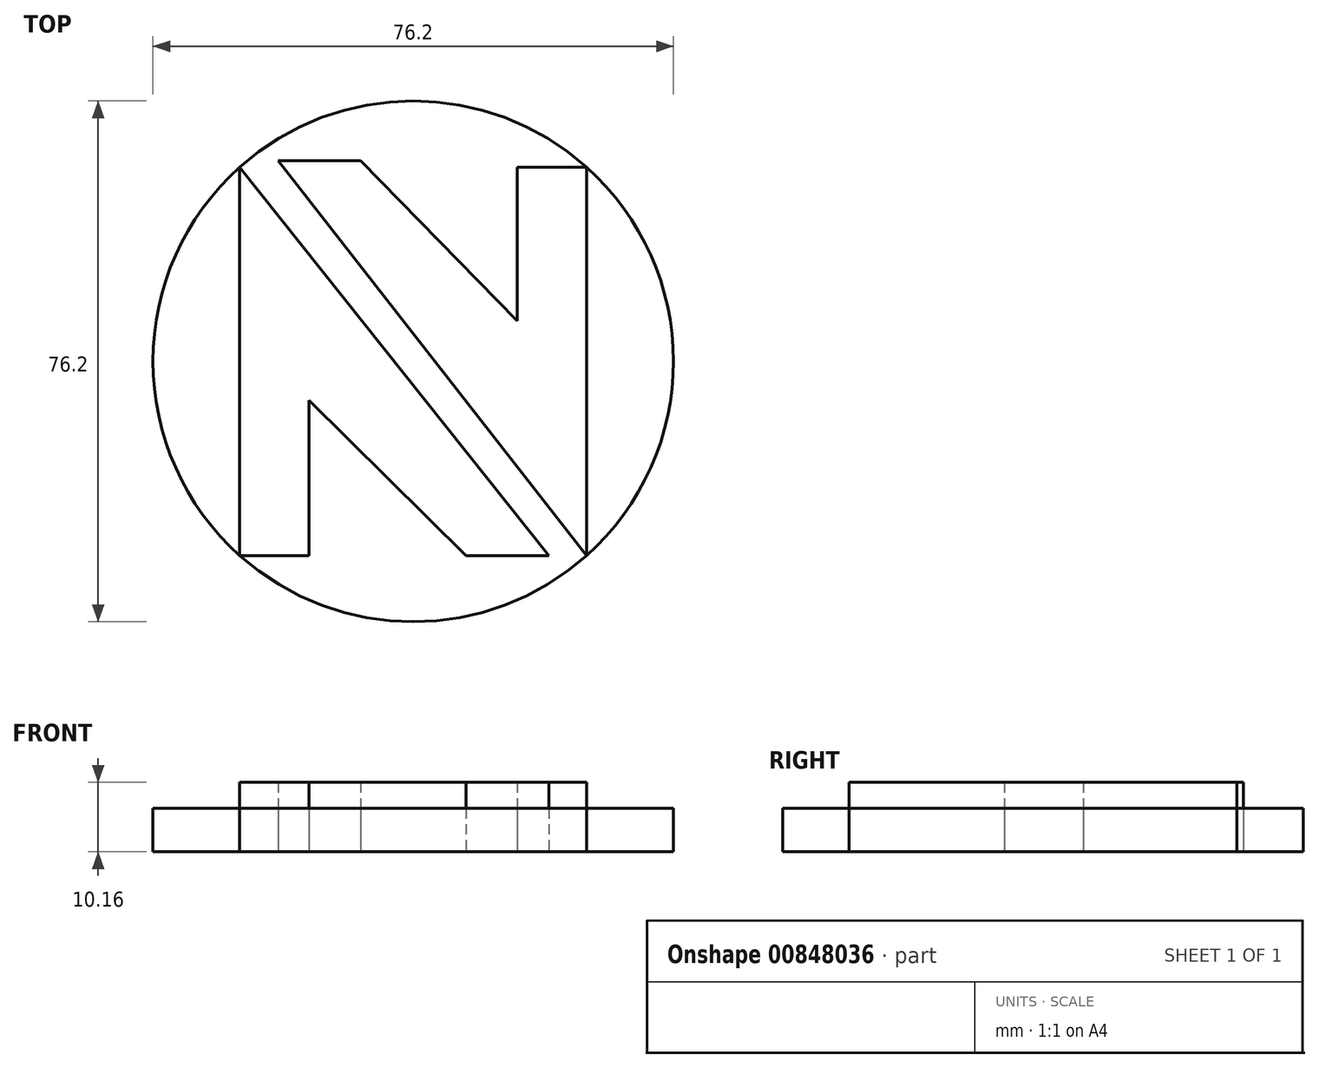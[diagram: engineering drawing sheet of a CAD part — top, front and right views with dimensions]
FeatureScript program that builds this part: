
annotation { "Feature Type Name" : "Feature", "Feature Type Description" : "" }
export const myFeature = defineFeature(function(context is Context, id is Id, definition is map)
    precondition{}
    {
        {
            var Q0;
            Q0=qCreatedBy(makeId("Top.planeOp"),FACE);
            var sketch = newSketch(context, id + "F0", { "sketchPlane" : qUnion([Q0])});
            skCircle(sketch, "E0", {"center": v(0, 0) * mm, "radius": 38.1 * mm});
            skLineSegment(sketch, "E1", {"start": v(-25.4, 28.4) * mm, "end": v(-25.4, -28.4) * mm});
            skLineSegment(sketch, "E2", {"start": v(-15.24, -5.68) * mm, "end": v(-15.24, -28.4) * mm});
            skLineSegment(sketch, "E3", {"start": v(-15.24, -28.4) * mm, "end": v(-25.4, -28.4) * mm});
            skLineSegment(sketch, "E4", {"start": v(-25.4, 28.4) * mm, "end": v(19.83, -28.4) * mm});
            skLineSegment(sketch, "E5", {"start": v(19.83, -28.4) * mm, "end": v(7.76, -28.4) * mm});
            skLineSegment(sketch, "E6", {"start": v(7.76, -28.4) * mm, "end": v(-15.24, -5.68) * mm});
            skLineSegment(sketch, "E7", {"start": v(25.4, -28.4) * mm, "end": v(25.4, 28.4) * mm});
            skLineSegment(sketch, "E8", {"start": v(25.4, -28.4) * mm, "end": v(-19.76, 29.33) * mm});
            skLineSegment(sketch, "E9", {"start": v(-19.76, 29.33) * mm, "end": v(-7.7, 29.33) * mm});
            skLineSegment(sketch, "E10", {"start": v(-7.7, 29.33) * mm, "end": v(15.24, 5.9) * mm});
            skLineSegment(sketch, "E11", {"start": v(15.24, 5.9) * mm, "end": v(15.24, 28.4) * mm});
            skLineSegment(sketch, "E12", {"start": v(15.24, 28.4) * mm, "end": v(25.4, 28.4) * mm});
            skSolve(sketch);
        }
        {
            var Q0;
            Q0=makeQuery(id+"F0.imprint","IMPRINT",FACE,{"disambiguationData":[TD([[makeQuery(id+"F0.imprint","IMPRINT",EDGE,{"derivedFrom":sQuery(id+"F0.wireOp",EDGE,"E7")}),1.0]])]});
            var Q1;
            Q1=makeQuery(id+"F0.imprint","IMPRINT",FACE,{"disambiguationData":[TD([[makeQuery(id+"F0.imprint","IMPRINT",EDGE,{"derivedFrom":sQuery(id+"F0.wireOp",EDGE,"E1")}),1.0]])]});
            extrude(context, id + "F1", {"entities" : qUnion([Q0, Q1]), "depth" : 10.16 * mm, "offsetDistance" : 25.4 * mm});
        }
        {
            var Q0;
            Q0=makeQuery(id+"F0.imprint","IMPRINT",FACE,{"disambiguationData":[TD([[makeQuery(id+"F0.imprint","IMPRINT",EDGE,{"derivedFrom":sQuery(id+"F0.wireOp",EDGE,"E2")}),1.0]])]});
            var Q1;
            {var subQ0=sQuery(id+"F0.wireOp",EDGE,"E1");Q1=makeQuery(id+"F0.imprint","IMPRINT",FACE,{"disambiguationData":[TD([[makeQuery(id+"F0.imprint","IMPRINT",EDGE,{"derivedFrom":subQ0}),-1.0]])]});}
            var Q2;
            {var subQ0=sQuery(id+"F0.wireOp",EDGE,"E7");Q2=makeQuery(id+"F0.imprint","IMPRINT",FACE,{"disambiguationData":[TD([[makeQuery(id+"F0.imprint","IMPRINT",EDGE,{"derivedFrom":subQ0}),-1.0]])]});}
            extrude(context, id + "F2", {"entities" : qUnion([Q0, Q1, Q2]), "depth" : 6.35 * mm, "offsetDistance" : 25.4 * mm});
        }
    });
